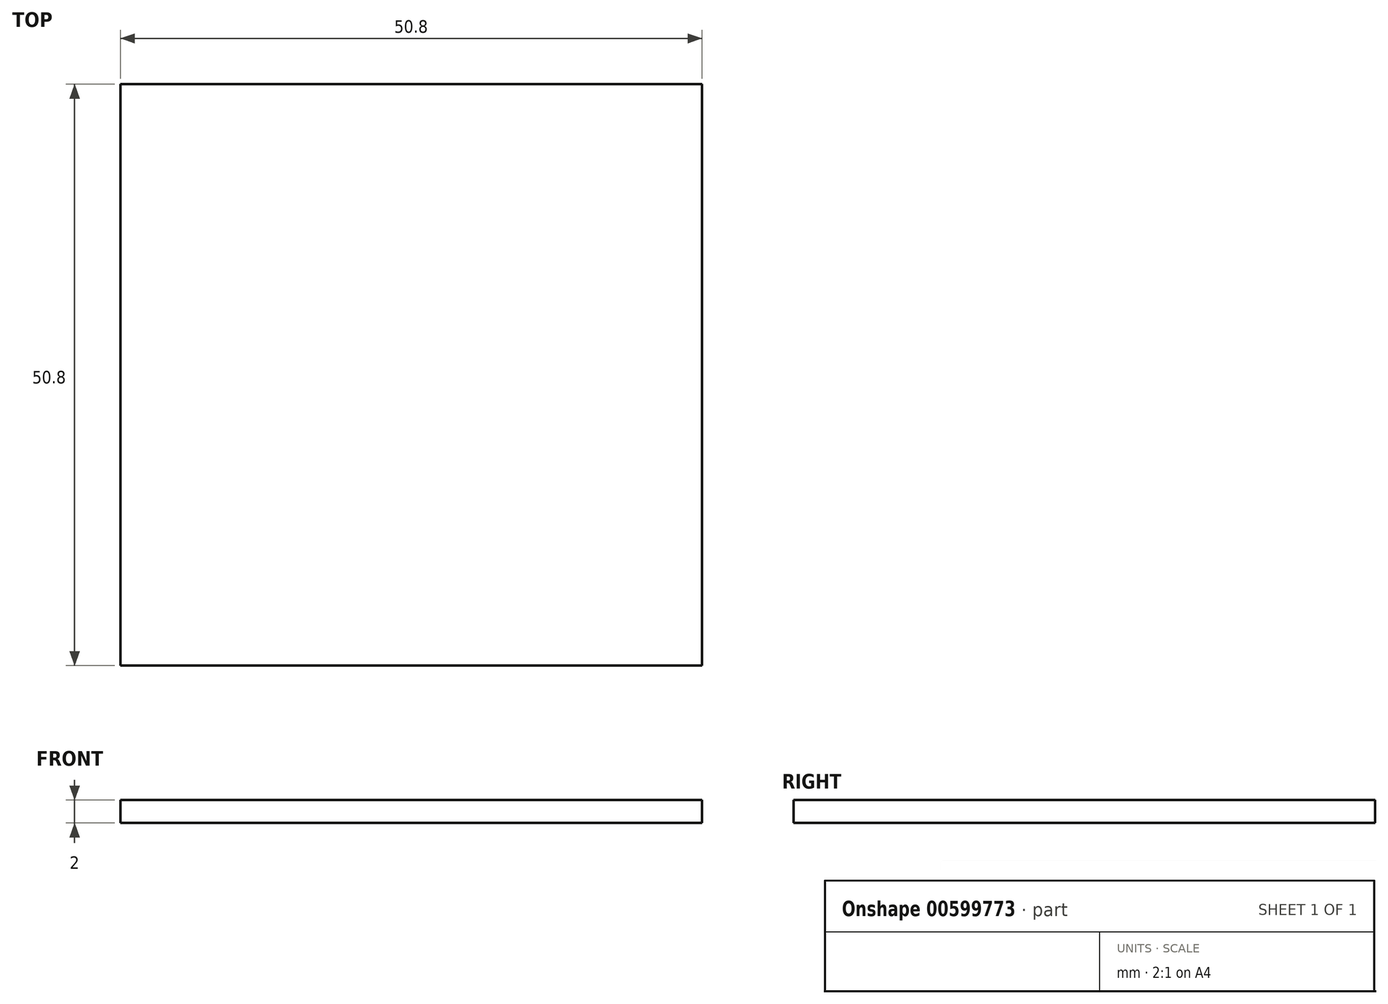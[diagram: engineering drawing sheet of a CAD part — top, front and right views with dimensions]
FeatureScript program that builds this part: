
annotation { "Feature Type Name" : "Feature", "Feature Type Description" : "" }
export const myFeature = defineFeature(function(context is Context, id is Id, definition is map)
    precondition{}
    {
        {
            var Q0;
            Q0=qCreatedBy(makeId("Top.planeOp"),FACE);
            var sketch = newSketch(context, id + "F0", { "sketchPlane" : qUnion([Q0])});
            skLineSegment(sketch, "E0.bottom", {"start": v(25.4, 25.4) * mm, "end": v(-25.4, 25.4) * mm});
            skLineSegment(sketch, "E0.top", {"start": v(25.4, -25.4) * mm, "end": v(-25.4, -25.4) * mm});
            skLineSegment(sketch, "E0.left", {"start": v(25.4, 25.4) * mm, "end": v(25.4, -25.4) * mm});
            skLineSegment(sketch, "E0.right", {"start": v(-25.4, 25.4) * mm, "end": v(-25.4, -25.4) * mm});
            skPoint(sketch, "E0.middle", {"position": v(0, 0) * mm});
            skSolve(sketch);
        }
        {
            var Q0;
            Q0 = qSketchRegion(id + "F0", true);
            extrude(context, id + "F1", {"entities" : qUnion([Q0]), "depth" : 2 * mm, "offsetDistance" : 25.4 * mm});
        }
    });
